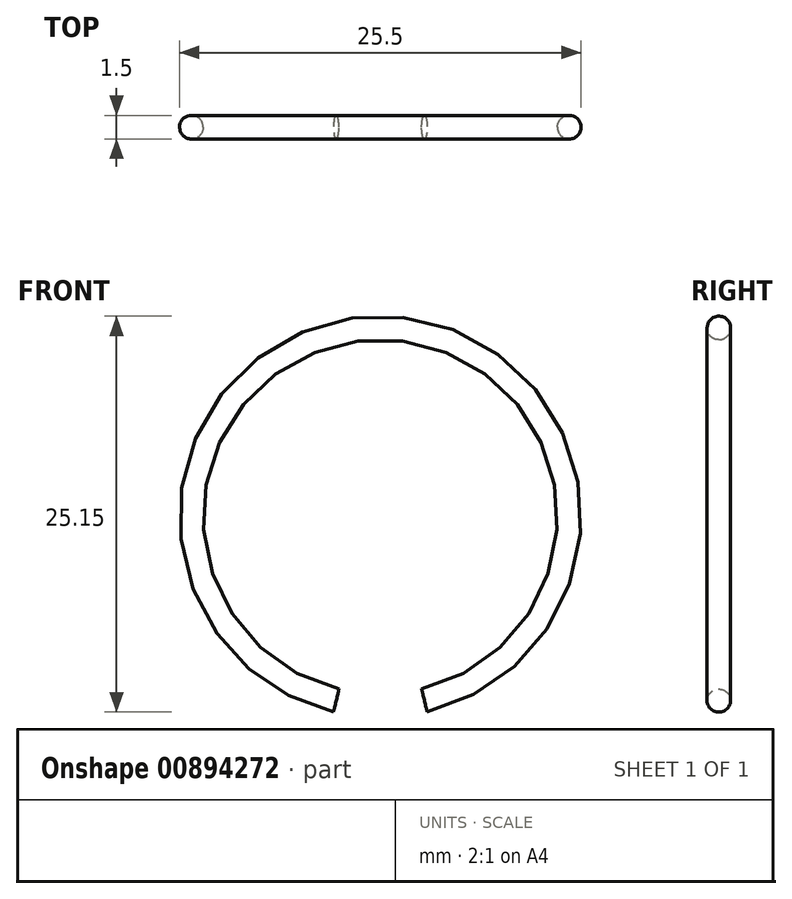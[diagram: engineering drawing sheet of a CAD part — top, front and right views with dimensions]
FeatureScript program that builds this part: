
annotation { "Feature Type Name" : "Feature", "Feature Type Description" : "" }
export const myFeature = defineFeature(function(context is Context, id is Id, definition is map)
    precondition{}
    {
        {
            var Q0;
            Q0=qCreatedBy(makeId("Right.planeOp"),FACE);
            var sketch = newSketch(context, id + "F0", { "sketchPlane" : qUnion([Q0])});
            skCircle(sketch, "E0", {"center": v(0, 12) * mm, "radius": 0.75 * mm});
            skLineSegment(sketch, "E1", {"start": v(0, 12) * mm, "end": v(0, 0) * mm, "construction": true});
            skLineSegment(sketch, "E2", {"start": v(0, 0) * mm, "end": v(-20, 0) * mm, "construction": true});
            skSolve(sketch);
        }
        {
            var Q0;
            Q0=makeQuery(id+"F0.imprint","IMPRINT",FACE,{"disambiguationData":[TD([[makeQuery(id+"F0.imprint","IMPRINT",EDGE,{"derivedFrom":sQuery(id+"F0.wireOp",EDGE,"E0")}),1.0]])]});
            var Q1;
            Q1=sQuery(id+"F0.wireOp",EDGE,"E0");
            var Q2;
            Q2=sQuery(id+"F0.wireOp",EDGE,"E2");
            revolve(context, id + "F1", {"surfaceOperationType" : NewSurfaceOperationType.NEW, "entities" : qUnion([Q0]), "surfaceEntities" : qUnion([Q1]), "axis" : qUnion([Q2]), "revolveType" : RevolveType.TWO_DIRECTIONS, "angle" : 166.5 * degree, "angleBack" : 193.5 * degree});
        }
    });
